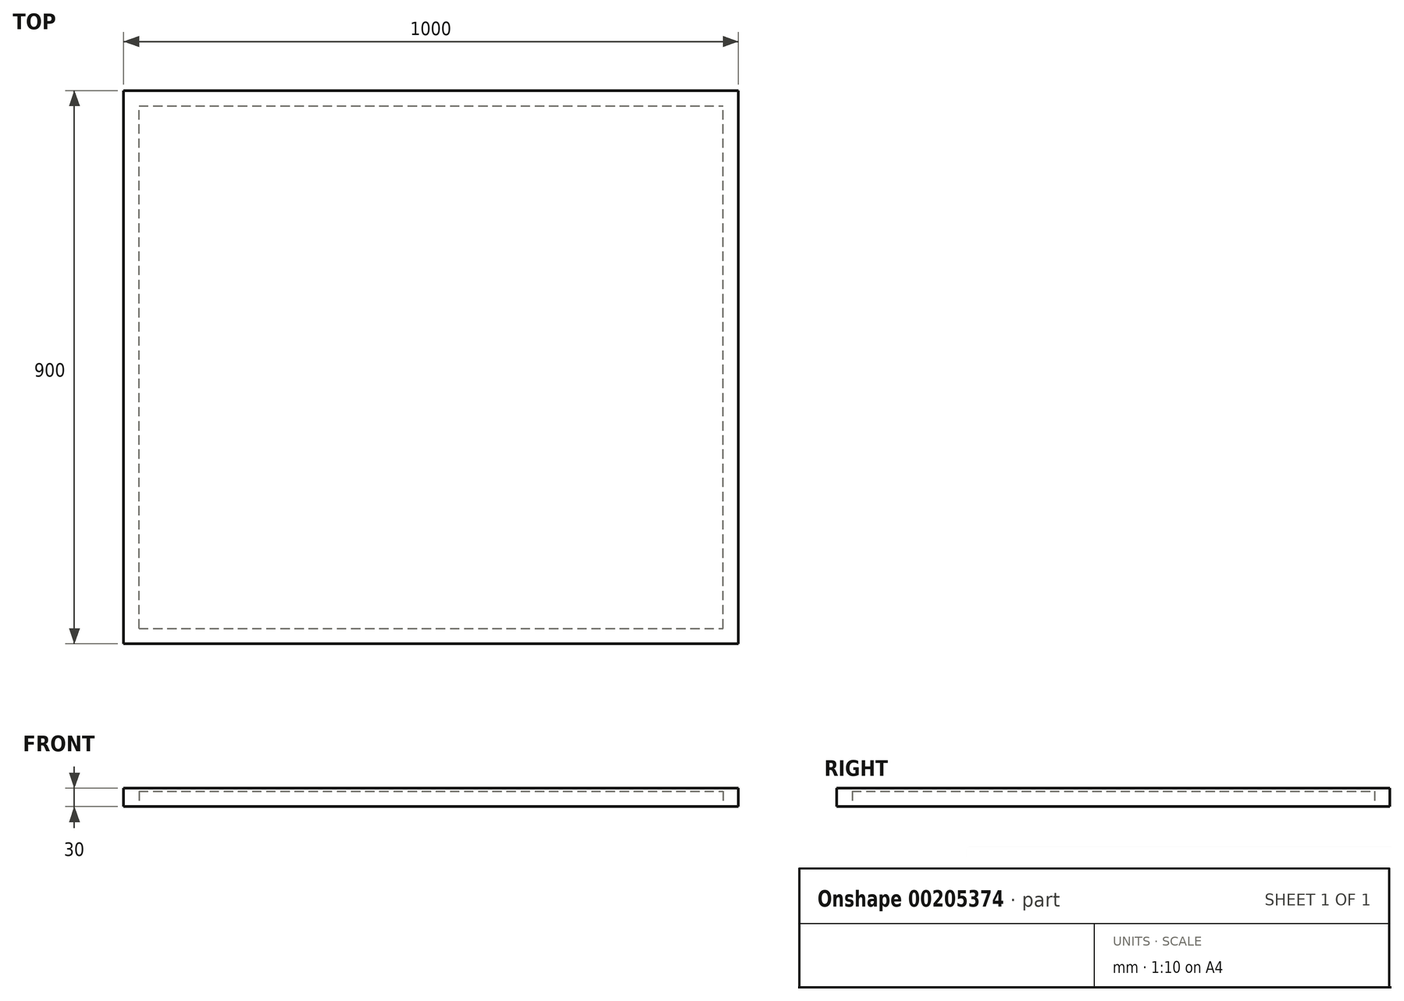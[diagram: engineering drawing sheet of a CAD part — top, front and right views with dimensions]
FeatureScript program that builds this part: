
annotation { "Feature Type Name" : "Feature", "Feature Type Description" : "" }
export const myFeature = defineFeature(function(context is Context, id is Id, definition is map)
    precondition{}
    {
        {
            var Q0;
            Q0=qCreatedBy(makeId("Top.planeOp"),FACE);
            var sketch = newSketch(context, id + "F0", { "sketchPlane" : qUnion([Q0])});
            skLineSegment(sketch, "E0.bottom", {"start": v(-500, -450) * mm, "end": v(500, -450) * mm});
            skLineSegment(sketch, "E0.top", {"start": v(-500, 450) * mm, "end": v(500, 450) * mm});
            skLineSegment(sketch, "E0.left", {"start": v(-500, -450) * mm, "end": v(-500, 450) * mm});
            skLineSegment(sketch, "E0.right", {"start": v(500, -450) * mm, "end": v(500, 450) * mm});
            skPoint(sketch, "E0.middle", {"position": v(0, 0) * mm});
            skSolve(sketch);
        }
        {
            var Q0;
            Q0 = qSketchRegion(id + "F0", true);
            extrude(context, id + "F1", {"entities" : qUnion([Q0]), "depth" : 30 * mm});
        }
        {
            var Q0;
            Q0=makeQuery(id+"F1.opExtrude","CAP_FACE",FACE,{"disambiguationData":[OSD([sQuery(id+"F0.wireOp",EDGE,"E0.bottom"),sQuery(id+"F0.wireOp",EDGE,"E0.top"),sQuery(id+"F0.wireOp",EDGE,"E0.left"),sQuery(id+"F0.wireOp",EDGE,"E0.right")])],"isStart":true});
            var sketch = newSketch(context, id + "F2", { "sketchPlane" : qUnion([Q0])});
            skLineSegment(sketch, "E1.0", {"start": v(-500, -450) * mm, "end": v(500, -450) * mm});
            skLineSegment(sketch, "E1.1", {"start": v(500, 450) * mm, "end": v(500, -450) * mm});
            skLineSegment(sketch, "E1.2", {"start": v(-500, 450) * mm, "end": v(500, 450) * mm});
            skLineSegment(sketch, "E1.3", {"start": v(-500, 450) * mm, "end": v(-500, -450) * mm});
            skLineSegment(sketch, "E2.0", {"start": v(-475, 425) * mm, "end": v(-475, -425) * mm});
            skLineSegment(sketch, "E2.1", {"start": v(-475, 425) * mm, "end": v(475, 425) * mm});
            skLineSegment(sketch, "E2.2", {"start": v(475, 425) * mm, "end": v(475, -425) * mm});
            skLineSegment(sketch, "E2.3", {"start": v(-475, -425) * mm, "end": v(475, -425) * mm});
            skSolve(sketch);
        }
        {
            var Q0;
            Q0=makeQuery(id+"F2.imprint","IMPRINT",FACE,{"disambiguationData":[TD([[makeQuery(id+"F2.imprint","IMPRINT",EDGE,{"derivedFrom":sQuery(id+"F2.wireOp",EDGE,"E2.0")}),1.0]])]});
            extrude(context, id + "F3", {"entities" : qUnion([Q0]), "operationType" : NewBodyOperationType.REMOVE, "oppositeDirection" : true, "depth" : 25 * mm});
        }
    });
